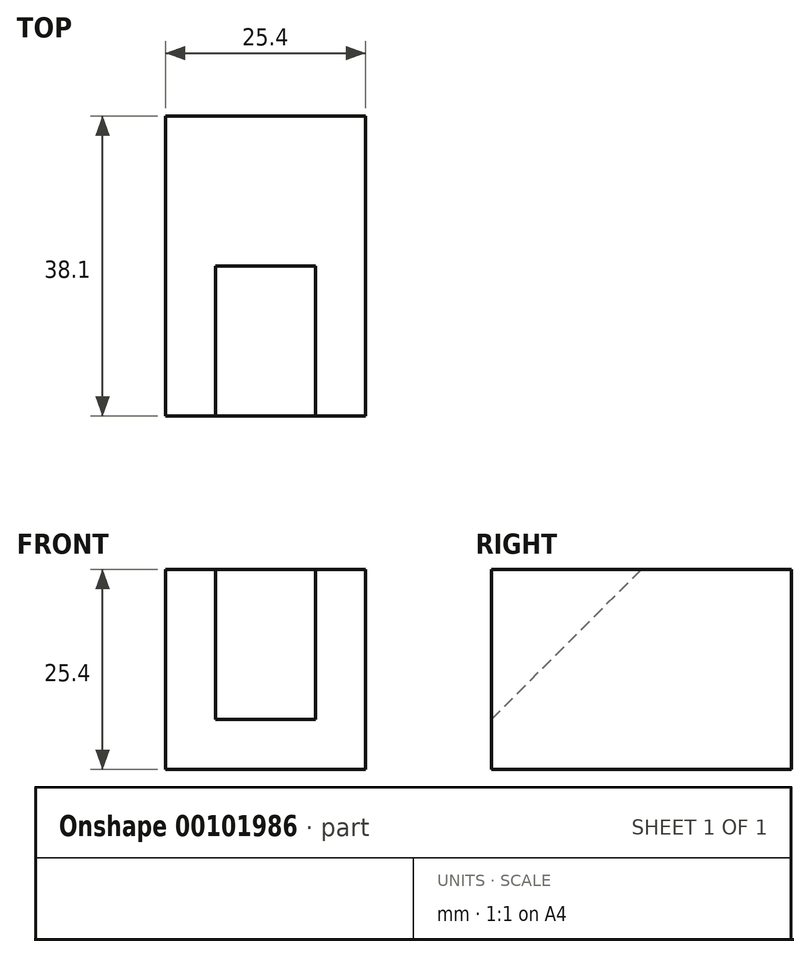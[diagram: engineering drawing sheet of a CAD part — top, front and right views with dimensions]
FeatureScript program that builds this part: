
annotation { "Feature Type Name" : "Feature", "Feature Type Description" : "" }
export const myFeature = defineFeature(function(context is Context, id is Id, definition is map)
    precondition{}
    {
        {
            var Q0;
            Q0=qCreatedBy(makeId("Right.planeOp"),FACE);
            var sketch = newSketch(context, id + "F0", { "sketchPlane" : qUnion([Q0])});
            skLineSegment(sketch, "E0", {"start": v(-20.27, 10.83) * mm, "end": v(-20.27, -14.57) * mm});
            skLineSegment(sketch, "E1", {"start": v(-20.27, -14.57) * mm, "end": v(17.83, -14.57) * mm});
            skLineSegment(sketch, "E2", {"start": v(17.83, -14.57) * mm, "end": v(17.83, 10.83) * mm});
            skLineSegment(sketch, "E3", {"start": v(17.83, 10.83) * mm, "end": v(-20.27, 10.83) * mm});
            skLineSegment(sketch, "E4", {"start": v(-20.27, -8.22) * mm, "end": v(-1.22, 10.83) * mm});
            skSolve(sketch);
        }
        {
            var Q0;
            Q0 = qSketchRegion(id + "F0", true);
            extrude(context, id + "F1", {"entities" : qUnion([Q0]), "oppositeDirection" : true, "depth" : 25.4 * mm});
        }
        {
            var Q0;
            {var subQ3=sQuery(id+"F0.wireOp",EDGE,"E4");Q0=makeQuery(id+"F0.imprint","IMPRINT",FACE,{"disambiguationData":[TD([[makeQuery(id+"F0.imprint","IMPRINT",EDGE,{"derivedFrom":subQ3}),1.0]])]});}
            extrude(context, id + "F2", {"entities" : qUnion([Q0]), "operationType" : NewBodyOperationType.REMOVE, "oppositeDirection" : true, "depth" : 19.05 * mm, "hasSecondDirection" : true, "secondDirectionOppositeDirection" : true, "secondDirectionDepth" : 6.35 * mm});
        }
    });
